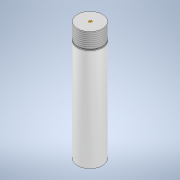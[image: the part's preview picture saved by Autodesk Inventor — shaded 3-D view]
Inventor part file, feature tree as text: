
AUTODESK INVENTOR PART (.ipt)
format: ipt  version: 2020 (Build 240168000, 168)  size: 113,664 bytes
history: native  units: mm
features: extrude x2, sketch x2, other x1, plane x1, thread x1
ambient origin geometry x8: Origin, YZ Plane, XZ Plane, XY Plane, X Axis, Y Axis, Z Axis, Center Point
bodies: Body1 (feature_tree)
feature tree (7):
  other  "Sólido1"
  extrude  "Extrusión1"  Depth=105.0mm TaperAngle=0.0deg
  plane  "Plano de trabajo1"
  extrude  "Extrusión2"  Depth=13.5mm
  thread  "Rosca1"  [1 undecoded]
  sketch  "Boceto1"  dims[d0=22.0mm d1=105.0mm d2=0.0mm]
  sketch  "Boceto2"  dims[d3=-13.5mm d4=20.0mm d5=1.0mm d6=0.0mm d7=13.5mm d8=0.0mm]
note: 1 required parameter value undecoded (feature->parameter linkage not recoverable at this tier; creation-order binding heuristic only, values carry confidence <= 0.55)
